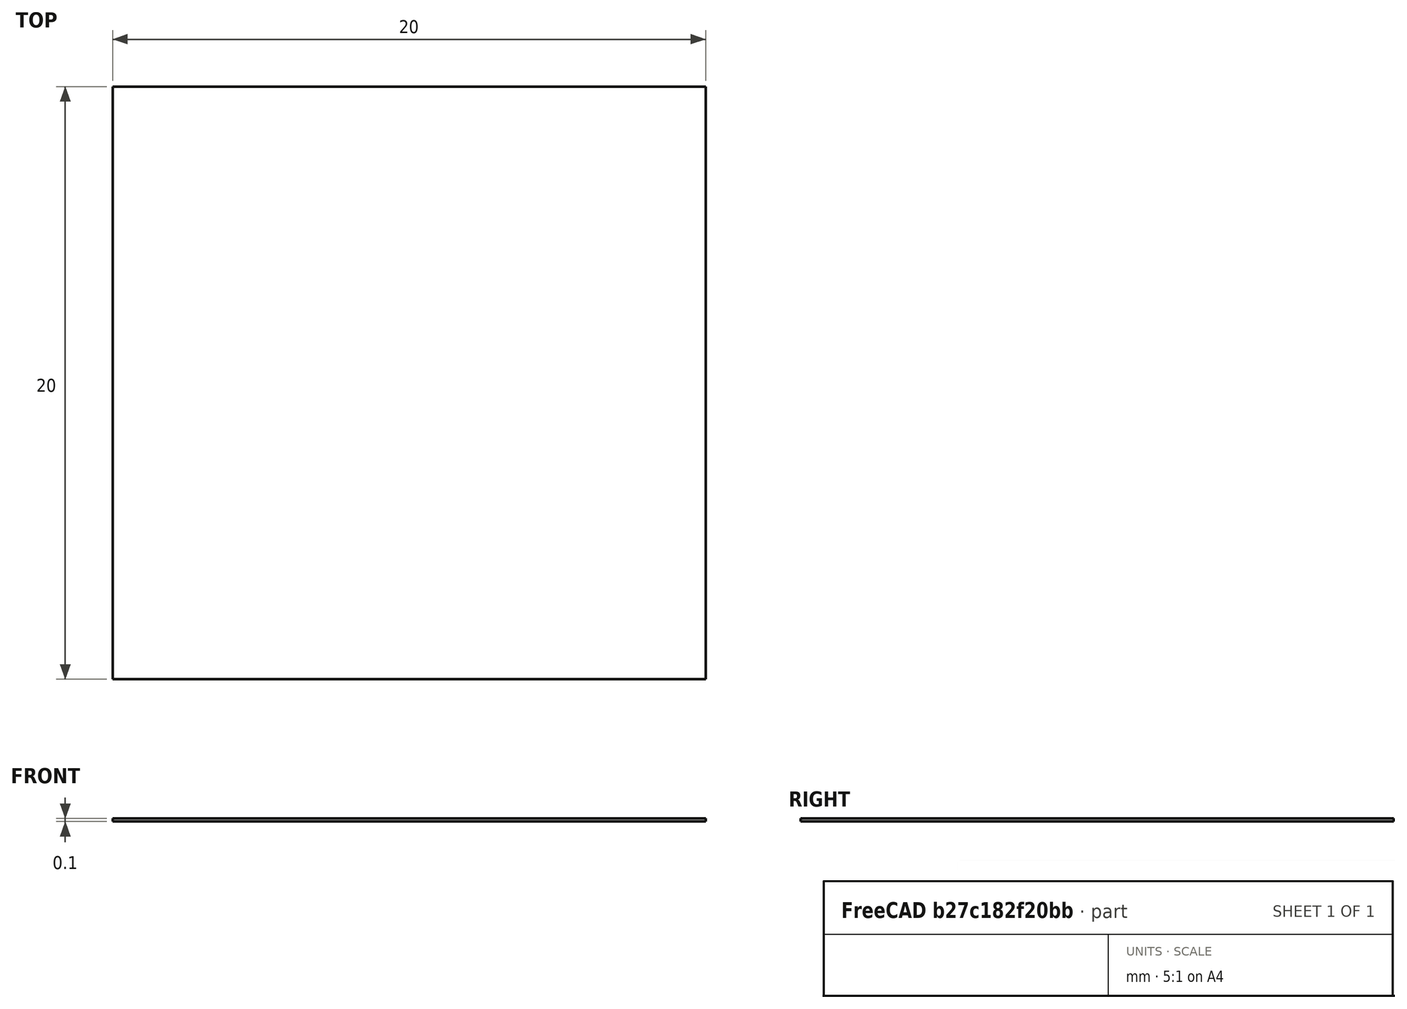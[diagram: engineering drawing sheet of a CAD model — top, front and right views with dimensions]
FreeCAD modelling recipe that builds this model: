
FCSTD DOCUMENT  (FreeCAD 0.16R)
Label: 20mmcube
License: All rights reserved
LicenseURL: http://en.wikipedia.org/wiki/All_rights_reserved
objects: Sketcher::SketchObject×1, PartDesign::Pad×1, Mesh::Feature×1
note: 3 computed .brp shape members not serialized (recipe doc carries the construction recipe); baked Part::Feature solids carry a one-line shape summary decoded from their .brp

FEATURE [Sketcher::SketchObject] Sketch
  sketch-geometry (4):
    g0: LineSegment StartX=-10 StartY=-10 StartZ=0 EndX=10 EndY=-10 EndZ=0
    g1: LineSegment StartX=10 StartY=-10 StartZ=0 EndX=10 EndY=10 EndZ=0
    g2: LineSegment StartX=10 StartY=10 StartZ=0 EndX=-10 EndY=10 EndZ=0
    g3: LineSegment StartX=-10 StartY=10 StartZ=0 EndX=-10 EndY=-10 EndZ=0
  constraints (11):
    c: Coincident(g0,g1)
    c: Coincident(g1,g2)
    c: Coincident(g2,g3)
    c: Coincident(g3,g0)
    c: Horizontal(g0)
    c: Horizontal(g2)
    c: Vertical(g1)
    c: Vertical(g3)
    c: Symmetric(g1,g0,g-1)
    c: DistanceX(g2,g2) = 20
    c: DistanceY(g1,g1) = 20
FEATURE [PartDesign::Pad] Pad
  Length = 0.1
  Length2 = 100
  Sketch = -> Sketch
  Type = 0
FEATURE [Mesh::Feature] Mesh  label="Pad (Meshed)"
